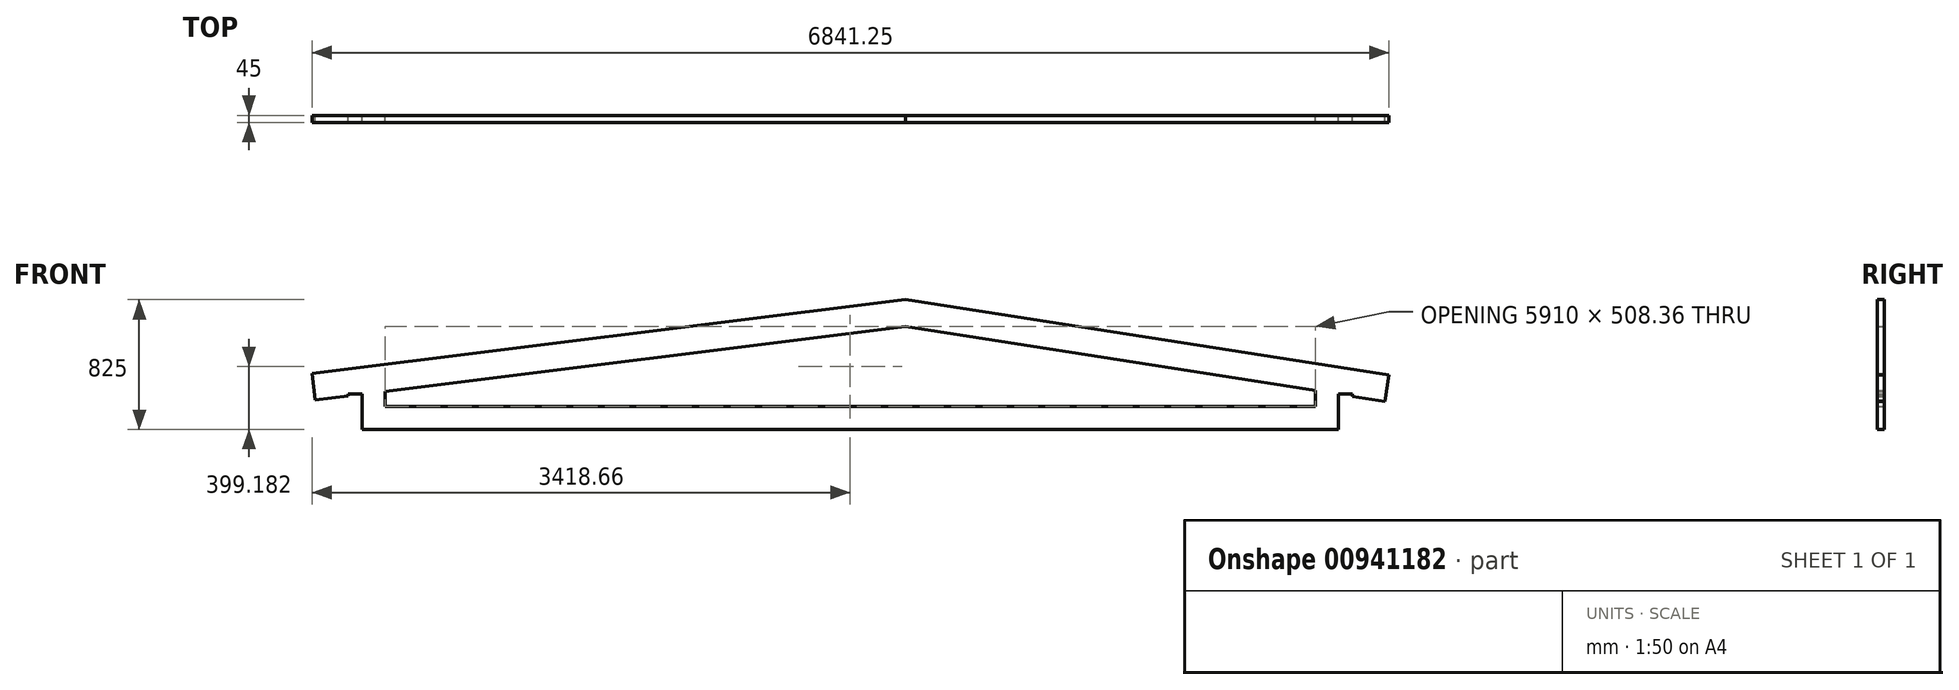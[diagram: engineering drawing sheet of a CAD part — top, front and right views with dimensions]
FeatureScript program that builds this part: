
annotation { "Feature Type Name" : "Feature", "Feature Type Description" : "" }
export const myFeature = defineFeature(function(context is Context, id is Id, definition is map)
    precondition{}
    {
        {
            var Q0;
            Q0=qCreatedBy(makeId("Front.planeOp"),FACE);
            var sketch = newSketch(context, id + "F0", { "sketchPlane" : qUnion([Q0])});
            skLineSegment(sketch, "E0", {"start": v(-3100, 0) * mm, "end": v(3100, 0) * mm});
            skLineSegment(sketch, "E1", {"start": v(-2955, 243) * mm, "end": v(350, 653.36) * mm});
            skLineSegment(sketch, "E2", {"start": v(350, 653.36) * mm, "end": v(2955, 247.59) * mm});
            skLineSegment(sketch, "E3", {"start": v(3100, 225) * mm, "end": v(3100, 0) * mm});
            skLineSegment(sketch, "E4", {"start": v(-3190, 225) * mm, "end": v(-3190, 213.83) * mm});
            skLineSegment(sketch, "E5", {"start": v(0, -1707.25) * mm, "end": v(0, 0) * mm, "construction": true});
            skLineSegment(sketch, "E6", {"start": v(-3100, 225) * mm, "end": v(-3190, 225) * mm});
            skLineSegment(sketch, "E7", {"start": v(352.66, 825) * mm, "end": v(-3418.66, 356.74) * mm});
            skLineSegment(sketch, "E8", {"start": v(-3418.66, 356.74) * mm, "end": v(-3397.71, 188.03) * mm});
            skLineSegment(sketch, "E9", {"start": v(-3397.71, 188.03) * mm, "end": v(-3190, 213.83) * mm});
            skLineSegment(sketch, "E10", {"start": v(-3100, 225) * mm, "end": v(-3100, 0) * mm});
            skLineSegment(sketch, "E11", {"start": v(-2955, 145) * mm, "end": v(2955, 145) * mm});
            skLineSegment(sketch, "E12", {"start": v(-2955, 145) * mm, "end": v(-2955, 243) * mm});
            skLineSegment(sketch, "E13.MirrorCS", {"start": v(3100, 225) * mm, "end": v(3190, 225) * mm});
            skLineSegment(sketch, "E14", {"start": v(3190, 210.98) * mm, "end": v(3396.43, 178.83) * mm});
            skLineSegment(sketch, "E15", {"start": v(2955, 145) * mm, "end": v(2955, 247.59) * mm});
            skLineSegment(sketch, "E16", {"start": v(3190, 225) * mm, "end": v(3190, 210.98) * mm});
            skLineSegment(sketch, "E17", {"start": v(3396.43, 178.83) * mm, "end": v(3422.6, 346.8) * mm});
            skLineSegment(sketch, "E18", {"start": v(3422.6, 346.8) * mm, "end": v(352.66, 825) * mm});
            skLineSegment(sketch, "E19", {"start": v(0, 0) * mm, "end": v(0, 2584.55) * mm, "construction": true});
            skSolve(sketch);
        }
        {
            var Q0;
            Q0 = qSketchRegion(id + "F0", true);
            extrude(context, id + "F1", {"entities" : qUnion([Q0]), "depth" : 45 * mm, "offsetDistance" : 25 * mm});
        }
    });
